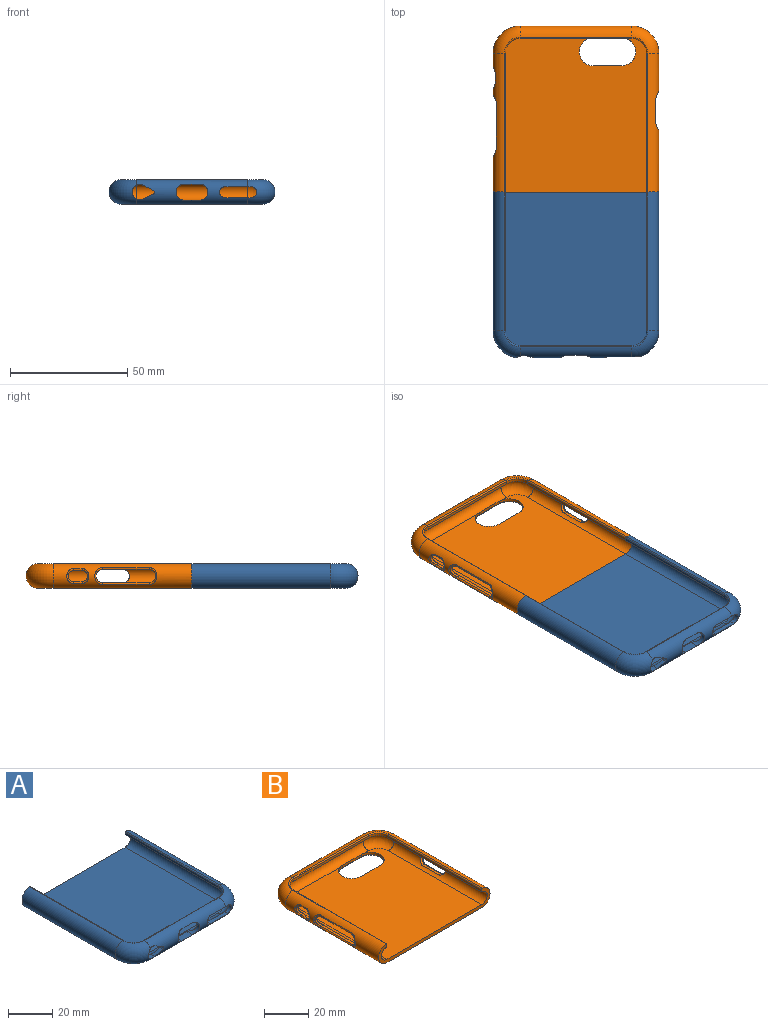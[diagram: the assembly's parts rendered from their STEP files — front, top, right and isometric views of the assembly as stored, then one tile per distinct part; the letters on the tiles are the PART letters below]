
ASSEMBLY  parts=2 mates=1
PART A: 35 faces, bbox 72.7x71.9x10.5 mm
  f0: plane 47.52x1.24mm, normal (0,1,0), area 59.1mm2, adj f13,f14,f16,f18
  f1: cylinder r=2.32mm len=4.65mm, axis (0,1,0), area 14.2mm2, adj f10,f12,f14,f20
  f2: plane 4.25x3.4mm, normal (-0.43,0,0.9), area 9.7mm2, adj f3,f5,f14,f20
  f3: cylinder r=1mm len=1.92mm, axis (0,1,0), area 4mm2, adj f2,f4,f14,f20
  f4: plane 4.25x3.19mm, normal (-0.43,0,-0.9), area 9.5mm2, adj f3,f5,f14,f20
  f5: cylinder r=3.25mm len=6.5mm, axis (0,1,0), area 30.6mm2, adj f2,f4,f14,f17,f19,f20
  f6: plane 6.85x3.59mm, normal (0,0,1), area 24.6mm2, adj f7,f9,f14,f20
  f7: cylinder r=3.4mm len=6.8mm, axis (0,1,0), area 24.7mm2, adj f6,f8,f14,f20
  f8: plane 6.85x3mm, normal (0,0,-1), area 20.5mm2, adj f7,f9,f14,f20
  f9: cylinder r=3.4mm len=6.8mm, axis (0,1,0), area 24.7mm2, adj f6,f8,f14,f20
  f10: plane 11.25x2.29mm, normal (0,0,1), area 24.3mm2, adj f1,f11,f14,f15,f20,f21
  f11: cylinder r=2.32mm len=4.65mm, axis (0,1,0), area 14.8mm2, adj f10,f12,f15,f21
  f12: plane 11.25x2.23mm, normal (0,0,-1), area 23.5mm2, adj f1,f11,f14,f15,f20,f21
  f13: cylinder r=0.51mm len=47.52mm, axis (-1,0,0), area 40.5mm2, adj f0,f20,f22,f23
  f14: cylinder r=3.5mm len=47.52mm, axis (-1,0,0), area 313.8mm2, adj f0,f1,f2,f3,f4,f5,f6,f7
  f15: torus R=6.37mm, axis (0,0,-1), area 131.1mm2, adj f10,f11,f12,f14,f16,f32,f33
  f16: cylinder r=6.37mm len=6.37mm, axis (0,0,-1), area 12.4mm2, adj f0,f15,f22,f31
  f17: torus R=6.37mm, axis (0,0,-1), area 140.1mm2, adj f5,f14,f18,f30,f33
  f18: cylinder r=6.37mm len=6.37mm, axis (0,0,-1), area 12.4mm2, adj f0,f17,f23,f29
  f19: torus R=6.37mm, axis (0,0,-1), area 239.7mm2, adj f5,f20,f23,f25,f26
  f20: cylinder r=5.28mm len=47.52mm, axis (-1,0,0), area 580mm2, adj f1,f2,f3,f4,f5,f6,f7,f8
  f21: torus R=6.37mm, axis (0,0,-1), area 231.1mm2, adj f10,f11,f12,f20,f22,f25,f28
  f22: torus R=6.88mm, axis (0,0,1), area 8.8mm2, adj f13,f16,f21,f27
  f23: torus R=6.88mm, axis (0,0,1), area 8.8mm2, adj f13,f18,f19,f24
  f24: cylinder r=0.51mm len=59.27mm, axis (0,1,0), area 50.5mm2, adj f23,f26,f29,f34
  f25: plane 65.64x60.26mm, normal (0,0,-1), area 3938.2mm2, adj f19,f20,f21,f26,f28,f34
  f26: cylinder r=5.28mm len=59.27mm, axis (0,1,0), area 949.4mm2, adj f19,f24,f25,f34
  f27: cylinder r=0.51mm len=59.27mm, axis (0,-1,0), area 50.5mm2, adj f22,f28,f31,f34
  f28: cylinder r=5.28mm len=59.27mm, axis (0,-1,0), area 949.4mm2, adj f21,f25,f27,f34
  f29: plane 59.27x1.24mm, normal (1,0,0), area 73.7mm2, adj f18,f24,f30,f34
  f30: cylinder r=3.5mm len=59.27mm, axis (0,1,0), area 651.7mm2, adj f17,f29,f33,f34
  f31: plane 59.27x1.24mm, normal (-1,0,0), area 73.7mm2, adj f16,f27,f32,f34
  f32: cylinder r=3.5mm len=59.27mm, axis (0,-1,0), area 651.7mm2, adj f15,f31,f33,f34
  f33: plane 65.64x60.26mm, normal (0,0,1), area 3938.2mm2, adj f14,f15,f17,f30,f32,f34
  f34: plane 70.82x10.53mm, normal (0,1,0), area 156mm2, adj f24,f25,f26,f27,f28,f29,f30,f31
PART B: 57 faces, bbox 72.7x71.9x10.6 mm
  f0: plane 65.64x60.26mm, normal (0,0,-1), area 3660.6mm2, adj f6,f7,f10,f17,f18,f23,f24,f25
  f1: cylinder r=3.5mm len=59.27mm, axis (0,-1,0), area 558.5mm2, adj f2,f4,f11,f40,f41,f42,f43,f56
  f2: plane 59.27x1.24mm, normal (-1,0,0), area 73.7mm2, adj f1,f8,f12,f56
  f3: cylinder r=3.5mm len=59.27mm, axis (0,1,0), area 456.4mm2, adj f4,f5,f15,f32,f33,f34,f35,f36
  f4: plane 65.64x60.26mm, normal (0,0,1), area 3684.1mm2, adj f1,f3,f11,f13,f15,f19,f20,f21
  f5: plane 59.27x1.24mm, normal (1,0,0), area 73.7mm2, adj f3,f9,f16,f56
  f6: cylinder r=5.28mm len=59.27mm, axis (0,-1,0), area 826.3mm2, adj f0,f8,f17,f44,f45,f46,f47,f56
  f7: cylinder r=5.28mm len=59.27mm, axis (0,1,0), area 691.2mm2, adj f0,f9,f18,f48,f49,f50,f51,f52
  f8: cylinder r=0.51mm len=59.27mm, axis (0,-1,0), area 50.5mm2, adj f2,f6,f29,f56
  f9: cylinder r=0.51mm len=59.27mm, axis (0,1,0), area 50.5mm2, adj f5,f7,f31,f56
  f10: cylinder r=5.28mm len=47.52mm, axis (1,0,0), area 747.4mm2, adj f0,f17,f18,f26,f27,f28,f30
  f11: torus R=6.37mm, axis (0,0,-1), area 148.5mm2, adj f1,f4,f12,f13
  f12: cylinder r=6.37mm len=6.37mm, axis (0,0,-1), area 12.4mm2, adj f2,f11,f14,f29
  f13: cylinder r=3.5mm len=47.52mm, axis (1,0,0), area 518.8mm2, adj f4,f11,f14,f15,f19,f20,f22
  f14: plane 47.52x1.24mm, normal (0,-1,0), area 59.1mm2, adj f12,f13,f16,f30
  f15: torus R=6.37mm, axis (0,0,-1), area 148.5mm2, adj f3,f4,f13,f16
  f16: cylinder r=6.37mm len=6.37mm, axis (0,0,-1), area 12.4mm2, adj f5,f14,f15,f31
  f17: torus R=6.37mm, axis (0,0,-1), area 247.6mm2, adj f0,f6,f10,f29
  f18: torus R=6.37mm, axis (0,0,-1), area 247.6mm2, adj f0,f7,f10,f31
  f19: cylinder r=6mm len=12mm, axis (0,0,1), area 23.9mm2, adj f4,f13,f21,f22,f24,f26
  f20: cylinder r=6mm len=12mm, axis (0,0,1), area 23.9mm2, adj f4,f13,f21,f22,f25,f27
  f21: plane 12.06x1.27mm, normal (0,1,0), area 15.3mm2, adj f4,f19,f20,f23
  f22: plane 12.06x1.22mm, normal (0,-1,0), area 14.7mm2, adj f13,f19,f20,f28
  f23: cylinder r=0.51mm len=12.06mm, axis (1,0,0), area 9.6mm2, adj f0,f21,f24,f25
  f24: torus R=6.51mm, axis (0,0,-1), area 13.1mm2, adj f0,f19,f23,f26
  f25: torus R=6.51mm, axis (0,0,-1), area 13.1mm2, adj f0,f20,f23,f27
  f26: bspline ~4.91x1.94mm, area 2.6mm2, adj f10,f19,f24,f28
  f27: bspline ~4.3x1.94mm, area 2.6mm2, adj f10,f20,f25,f28
  f28: cylinder r=0.51mm len=12.06mm, axis (1,0,0), area 10.6mm2, adj f10,f22,f26,f27
  f29: torus R=6.88mm, axis (0,0,1), area 8.8mm2, adj f8,f12,f17,f30
  f30: cylinder r=0.51mm len=47.52mm, axis (1,0,0), area 40.5mm2, adj f10,f14,f29,f31
  f31: torus R=6.88mm, axis (0,0,1), area 8.8mm2, adj f9,f16,f18,f30
  f32: cylinder r=2.39mm len=4.77mm, axis (1,0,0), area 9.3mm2, adj f3,f33,f35,f55
  f33: plane 3.63x1.22mm, normal (0,0,-1), area 4.4mm2, adj f3,f32,f34,f53
  f34: cylinder r=2.39mm len=4.77mm, axis (1,0,0), area 9.3mm2, adj f3,f33,f35,f52
  f35: plane 3.63x1.24mm, normal (0,0,1), area 4.5mm2, adj f3,f32,f34,f54
  f36: cylinder r=2.8mm len=5.59mm, axis (1,0,0), area 11.3mm2, adj f3,f37,f39,f51
  f37: plane 20.01x1.32mm, normal (0,0,-1), area 26.4mm2, adj f3,f36,f38,f49
  f38: cylinder r=2.8mm len=5.59mm, axis (1,0,0), area 11.3mm2, adj f3,f37,f39,f48
  f39: plane 20.01x1.36mm, normal (0,0,1), area 27.1mm2, adj f3,f36,f38,f50
  f40: plane 10.2x1.32mm, normal (0,0,-1), area 13.4mm2, adj f1,f41,f43,f47
  f41: cylinder r=2.79mm len=5.59mm, axis (-1,0,0), area 11.3mm2, adj f1,f40,f42,f46
  f42: plane 10.2x1.35mm, normal (0,0,1), area 13.8mm2, adj f1,f41,f43,f44
  f43: cylinder r=2.79mm len=5.59mm, axis (-1,0,0), area 11.3mm2, adj f1,f40,f42,f45
  f44: cylinder r=0.51mm len=10.2mm, axis (0,-1,0), area 12.2mm2, adj f6,f42,f45,f46
  f45: bspline ~7.31x3.93mm, area 9.8mm2, adj f6,f43,f44,f47
  f46: bspline ~7.31x3.94mm, area 9.8mm2, adj f6,f41,f44,f47
  f47: cylinder r=0.51mm len=10.2mm, axis (0,-1,0), area 12mm2, adj f6,f40,f45,f46
  f48: bspline ~7.31x3.94mm, area 9.8mm2, adj f7,f38,f49,f50
  f49: cylinder r=0.51mm len=20.01mm, axis (0,1,0), area 23.6mm2, adj f7,f37,f48,f51
  f50: cylinder r=0.51mm len=20.01mm, axis (0,1,0), area 23.9mm2, adj f7,f39,f48,f51
  f51: bspline ~7.31x3.94mm, area 9.8mm2, adj f7,f36,f49,f50
  f52: bspline ~6.41x3.47mm, area 8.2mm2, adj f7,f34,f53,f54
  f53: cylinder r=0.51mm len=3.63mm, axis (0,1,0), area 4.1mm2, adj f7,f33,f52,f55
  f54: cylinder r=0.51mm len=3.63mm, axis (0,1,0), area 4.1mm2, adj f7,f35,f52,f55
  f55: bspline ~6.41x3.48mm, area 8.2mm2, adj f7,f32,f53,f54
  f56: plane 70.82x10.53mm, normal (0,-1,0), area 156mm2, adj f0,f1,f2,f3,f4,f5,f6,f7
PLACE A t=(-35.99,3.87,-21.1)mm
PLACE B t=(-35.99,3.87,-21.1)mm
MATE fastened B.f56 <-> A.f34  axis (0,-1,0) through (-35.99,3.87,-21.65)mm
